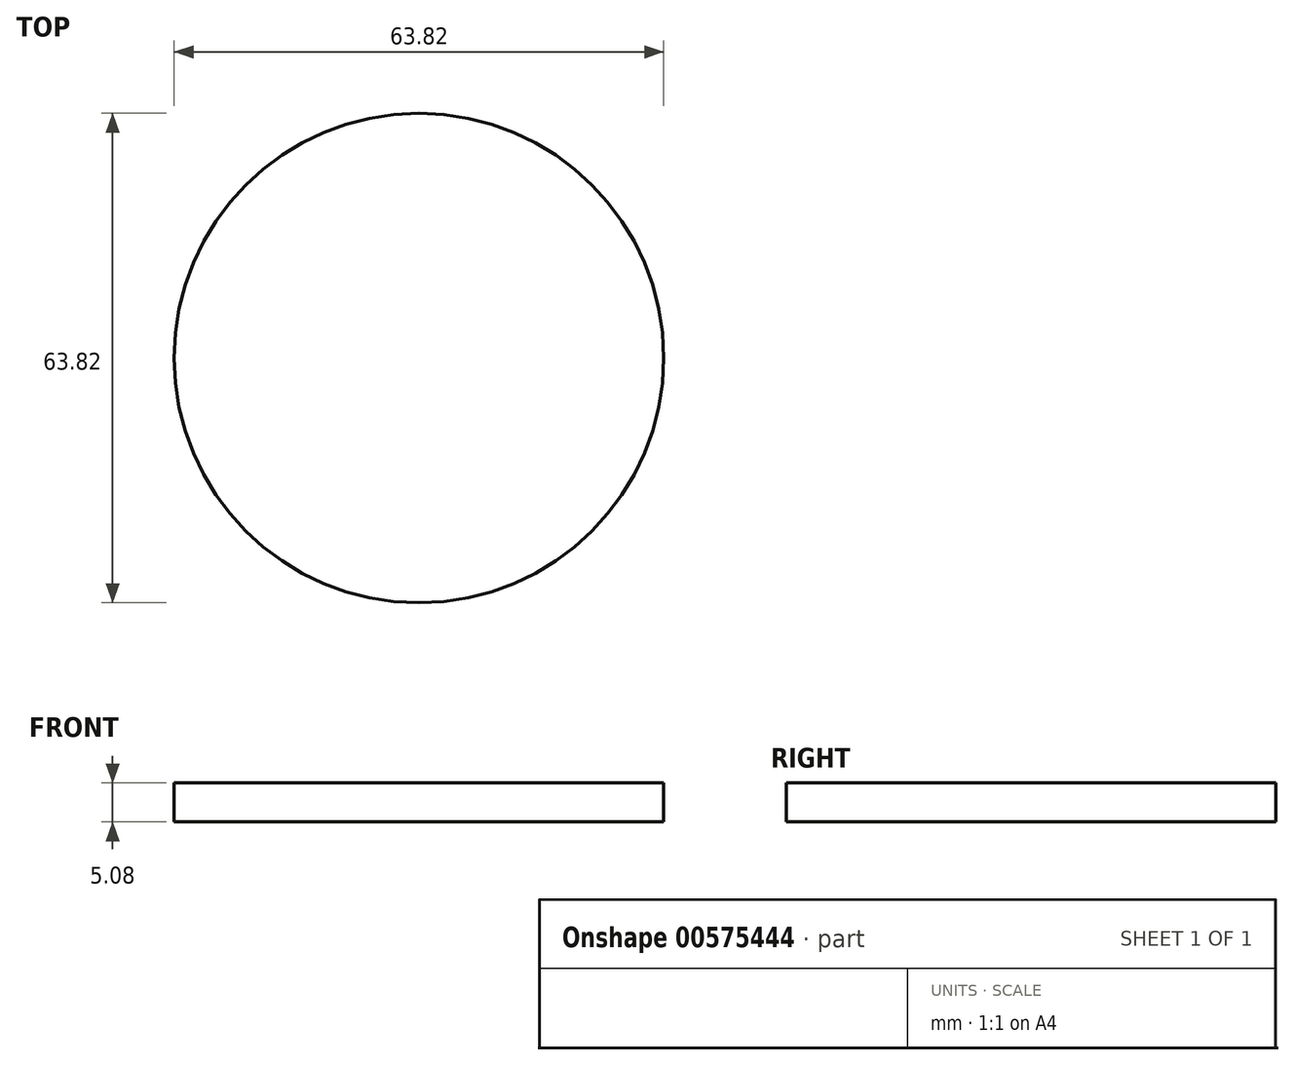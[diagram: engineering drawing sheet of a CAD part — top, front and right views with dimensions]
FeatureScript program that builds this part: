
annotation { "Feature Type Name" : "Feature", "Feature Type Description" : "" }
export const myFeature = defineFeature(function(context is Context, id is Id, definition is map)
    precondition{}
    {
        {
            var Q0;
            Q0=qCreatedBy(makeId("Top.planeOp"),FACE);
            var sketch = newSketch(context, id + "F0", { "sketchPlane" : qUnion([Q0])});
            skCircle(sketch, "E0", {"center": v(0, 0) * mm, "radius": 31.9 * mm});
            skSolve(sketch);
        }
        {
            var Q0;
            Q0=makeQuery(id+"F0.imprint","IMPRINT",FACE,{"disambiguationData":[TD([[makeQuery(id+"F0.imprint","IMPRINT",EDGE,{"derivedFrom":sQuery(id+"F0.wireOp",EDGE,"E0")}),1.0]])]});
            extrude(context, id + "F1", {"entities" : qUnion([Q0]), "depth" : 5.08 * mm, "offsetDistance" : 25.4 * mm});
        }
    });
